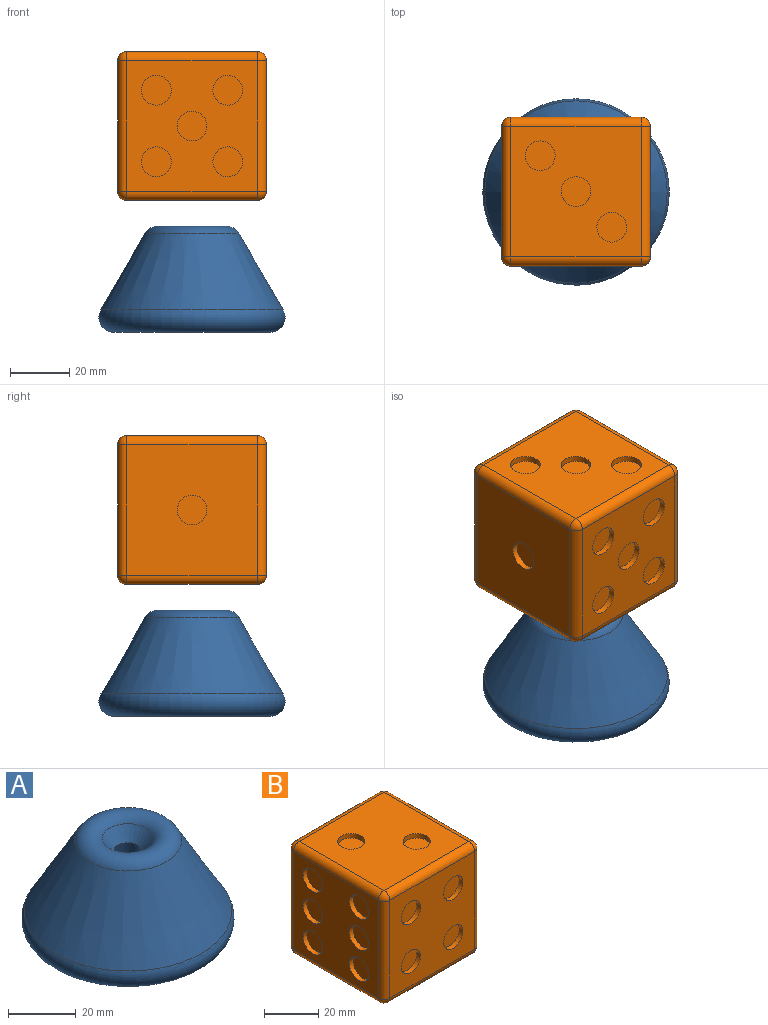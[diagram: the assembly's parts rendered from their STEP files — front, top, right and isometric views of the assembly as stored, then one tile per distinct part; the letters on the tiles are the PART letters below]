
ASSEMBLY  parts=2 mates=1
PART A: 6 faces, bbox 67.8x67.8x35.7 mm
  f0: cone r=12.13mm half-angle=38deg, axis (0,0,1), area 205.2mm2, adj f3,f4
  f1: cone r=12.13mm half-angle=30deg, axis (0,0,-1), area 4335.3mm2, adj f4,f5
  f2: plane 52.68x52.68mm, normal (0,0,-1), area 1871.5mm2, adj f3,f5
  f3: cone r=4.12mm half-angle=11.1deg, axis (0,0,-1), area 1318.9mm2, adj f0,f2
  f4: torus R=11.5mm, axis (0,0,-1), area 724.5mm2, adj f0,f1
  f5: torus R=26.34mm, axis (0,0,-1), area 1968.7mm2, adj f1,f2
PART B: 68 faces, bbox 50x50x50 mm
  f0: plane 44x44mm, normal (0,-1,0), area 1621.8mm2, adj f40,f42,f44,f46,f48,f52,f53,f54
  f1: plane 44x44mm, normal (-1,0,0), area 1464.8mm2, adj f8,f10,f12,f14,f16,f18,f53,f62
  f2: plane 44x44mm, normal (0,1,0), area 1700.4mm2, adj f20,f22,f24,f56,f61,f64,f67
  f3: plane 44x44mm, normal (1,0,0), area 1857.5mm2, adj f6,f48,f51,f55,f56
  f4: plane 44x44mm, normal (0,0,1), area 1778.9mm2, adj f36,f38,f51,f52,f61,f62
  f5: plane 44x44mm, normal (0,0,-1), area 1543.3mm2, adj f26,f28,f30,f32,f34,f54,f55,f63
  f6: cylinder r=5mm len=10mm, axis (1,0,0), area 62.8mm2, adj f3,f7
  f7: plane 10x10mm, normal (1,0,0), area 78.5mm2, adj f6
  f8: cylinder r=5mm len=10mm, axis (-1,0,0), area 62.8mm2, adj f1,f9
  f9: plane 10x10mm, normal (-1,0,0), area 78.5mm2, adj f8
  f10: cylinder r=5mm len=10mm, axis (-1,0,0), area 62.8mm2, adj f1,f11
  f11: plane 10x10mm, normal (-1,0,0), area 78.5mm2, adj f10
  f12: cylinder r=5mm len=10mm, axis (-1,0,0), area 62.8mm2, adj f1,f13
  f13: plane 10x10mm, normal (-1,0,0), area 78.5mm2, adj f12
  f14: cylinder r=5mm len=10mm, axis (-1,0,0), area 62.8mm2, adj f1,f15
  f15: plane 10x10mm, normal (-1,0,0), area 78.5mm2, adj f14
  f16: cylinder r=5mm len=10mm, axis (-1,0,0), area 62.8mm2, adj f1,f17
  f17: plane 10x10mm, normal (-1,0,0), area 78.5mm2, adj f16
  f18: cylinder r=5mm len=10mm, axis (-1,0,0), area 62.8mm2, adj f1,f19
  f19: plane 10x10mm, normal (-1,0,0), area 78.5mm2, adj f18
  f20: cylinder r=5mm len=10mm, axis (0,1,0), area 62.8mm2, adj f2,f21
  f21: plane 10x10mm, normal (0,1,0), area 78.5mm2, adj f20
  f22: cylinder r=5mm len=10mm, axis (0,1,0), area 62.8mm2, adj f2,f23
  f23: plane 10x10mm, normal (0,1,0), area 78.5mm2, adj f22
  f24: cylinder r=5mm len=10mm, axis (0,1,0), area 62.8mm2, adj f2,f25
  f25: plane 10x10mm, normal (0,1,0), area 78.5mm2, adj f24
  f26: cylinder r=5mm len=10mm, axis (0,0,-1), area 62.8mm2, adj f5,f27
  f27: plane 10x10mm, normal (0,0,-1), area 78.5mm2, adj f26
  f28: cylinder r=5mm len=10mm, axis (0,0,-1), area 62.8mm2, adj f5,f29
  f29: plane 10x10mm, normal (0,0,-1), area 78.5mm2, adj f28
  f30: cylinder r=5mm len=10mm, axis (0,0,-1), area 62.8mm2, adj f5,f31
  f31: plane 10x10mm, normal (0,0,-1), area 78.5mm2, adj f30
  f32: cylinder r=5mm len=10mm, axis (0,0,-1), area 62.8mm2, adj f5,f33
  f33: plane 10x10mm, normal (0,0,-1), area 78.5mm2, adj f32
  f34: cylinder r=5mm len=10mm, axis (0,0,-1), area 62.8mm2, adj f5,f35
  f35: plane 10x10mm, normal (0,0,-1), area 78.5mm2, adj f34
  f36: cylinder r=5mm len=10mm, axis (0,0,1), area 62.8mm2, adj f4,f37
  f37: plane 10x10mm, normal (0,0,1), area 78.5mm2, adj f36
  f38: cylinder r=5mm len=10mm, axis (0,0,1), area 62.8mm2, adj f4,f39
  f39: plane 10x10mm, normal (0,0,1), area 78.5mm2, adj f38
  f40: cylinder r=5mm len=10mm, axis (0,-1,0), area 62.8mm2, adj f0,f41
  f41: plane 10x10mm, normal (0,-1,0), area 78.5mm2, adj f40
  f42: cylinder r=5mm len=10mm, axis (0,-1,0), area 62.8mm2, adj f0,f43
  f43: plane 10x10mm, normal (0,-1,0), area 78.5mm2, adj f42
  f44: cylinder r=5mm len=10mm, axis (0,-1,0), area 62.8mm2, adj f0,f45
  f45: plane 10x10mm, normal (0,-1,0), area 78.5mm2, adj f44
  f46: cylinder r=5mm len=10mm, axis (0,-1,0), area 62.8mm2, adj f0,f47
  f47: plane 10x10mm, normal (0,-1,0), area 78.5mm2, adj f46
  f48: cylinder r=3mm len=44mm, axis (0,0,1), area 207.3mm2, adj f0,f3,f49,f50
  f49: sphere r=3mm, area 14.1mm2, adj f48,f51,f52
  f50: sphere r=3mm, area 14.1mm2, adj f48,f54,f55
  f51: cylinder r=3mm len=44mm, axis (0,-1,0), area 207.3mm2, adj f3,f4,f49,f57
  f52: cylinder r=3mm len=44mm, axis (-1,0,0), area 207.3mm2, adj f0,f4,f49,f58
  f53: cylinder r=3mm len=44mm, axis (0,0,-1), area 207.3mm2, adj f0,f1,f58,f59
  f54: cylinder r=3mm len=44mm, axis (1,0,0), area 207.3mm2, adj f0,f5,f50,f59
  f55: cylinder r=3mm len=44mm, axis (0,1,0), area 207.3mm2, adj f3,f5,f50,f60
  f56: cylinder r=3mm len=44mm, axis (0,0,-1), area 207.3mm2, adj f2,f3,f57,f60
  f57: sphere r=3mm, area 14.1mm2, adj f51,f56,f61
  f58: sphere r=3mm, area 14.1mm2, adj f52,f53,f62
  f59: sphere r=3mm, area 14.1mm2, adj f53,f54,f63
  f60: sphere r=3mm, area 14.1mm2, adj f55,f56,f64
  f61: cylinder r=3mm len=44mm, axis (1,0,0), area 207.3mm2, adj f2,f4,f57,f65
  f62: cylinder r=3mm len=44mm, axis (0,1,0), area 207.3mm2, adj f1,f4,f58,f65
  f63: cylinder r=3mm len=44mm, axis (0,-1,0), area 207.3mm2, adj f1,f5,f59,f66
  f64: cylinder r=3mm len=44mm, axis (-1,0,0), area 207.3mm2, adj f2,f5,f60,f66
  f65: sphere r=3mm, area 14.1mm2, adj f61,f62,f67
  f66: sphere r=3mm, area 14.1mm2, adj f63,f64,f67
  f67: cylinder r=3mm len=44mm, axis (0,0,1), area 207.3mm2, adj f1,f2,f65,f66
PLACE A at identity fixed
PLACE B rot(axis=(0,0.71,0.71),180deg) t=(0,0,69.37)mm
MATE fastened A.f5 <-> B.f22  axis (0,0,-1) through (0,0,29.37)mm
